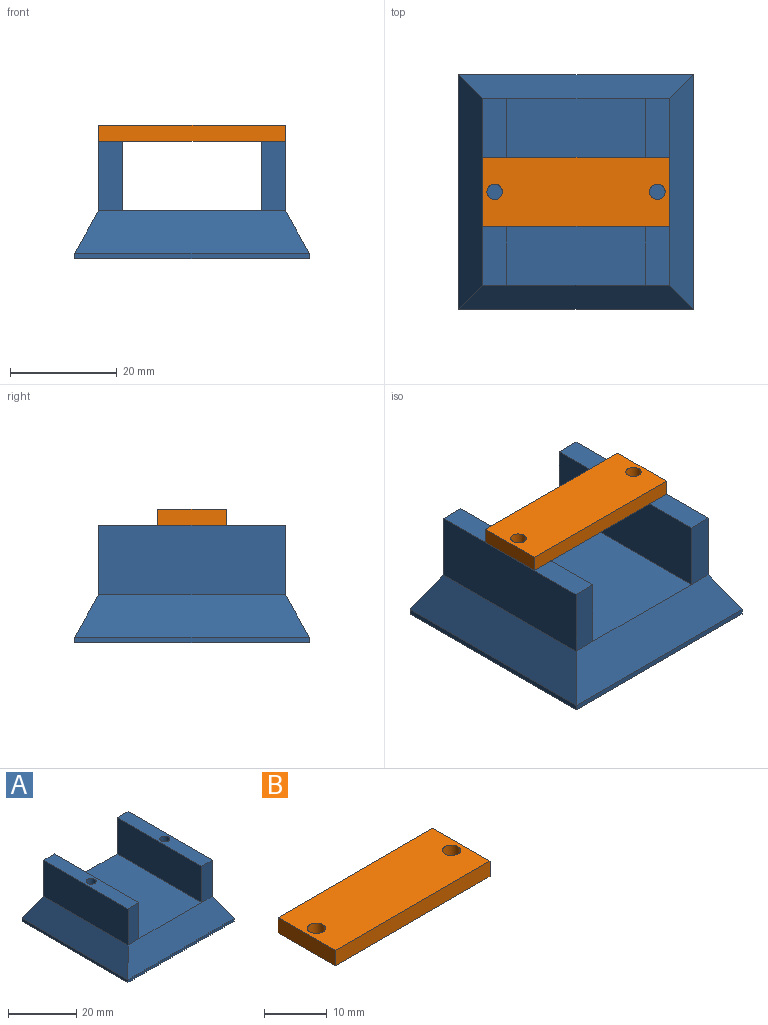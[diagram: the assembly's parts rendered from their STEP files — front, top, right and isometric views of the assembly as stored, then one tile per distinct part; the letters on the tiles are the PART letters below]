
ASSEMBLY  parts=2 mates=1
PART A: 33 faces, bbox 44x44x22 mm
  f0: plane 35x26mm, normal (0,0,1), area 910mm2, adj f7,f8,f19,f25
  f1: plane 44x1mm, normal (-1,0,0), area 44mm2, adj f2,f4,f5,f6
  f2: plane 44x1mm, normal (0,-1,0), area 44mm2, adj f1,f3,f5,f8
  f3: plane 44x1mm, normal (1,0,0), area 44mm2, adj f2,f4,f5,f9
  f4: plane 44x1mm, normal (0,1,0), area 44mm2, adj f1,f3,f5,f7
  f5: plane 44x44mm, normal (0,0,-1), area 492mm2, adj f1,f2,f3,f4,f10,f11,f12,f13
  f6: plane 44x8mm, normal (-0.87,0,0.49), area 362.6mm2, adj f1,f7,f8,f27
  f7: plane 44x8mm, normal (0,0.87,0.49), area 362.6mm2, adj f0,f4,f6,f9,f22,f26
  f8: plane 44x8mm, normal (0,-0.87,0.49), area 362.6mm2, adj f0,f2,f6,f9,f20,f24
  f9: plane 44x8mm, normal (0.87,0,0.49), area 362.6mm2, adj f3,f7,f8,f21
  f10: plane 38x0.21mm, normal (1,0,0), area 8.1mm2, adj f5,f11,f13,f15
  f11: plane 38x0.21mm, normal (0,1,0), area 8.1mm2, adj f5,f10,f12,f17
  f12: plane 38x0.21mm, normal (-1,0,0), area 8.1mm2, adj f5,f11,f13,f18
  f13: plane 38x0.21mm, normal (0,-1,0), area 8.1mm2, adj f5,f10,f12,f16
  f14: plane 31.49x31.49mm, normal (0,0,-1), area 991.7mm2, adj f15,f16,f17,f18
  f15: plane 38x5.79mm, normal (0.87,0,-0.49), area 230.7mm2, adj f10,f14,f16,f17
  f16: plane 38x5.79mm, normal (0,-0.87,-0.49), area 230.7mm2, adj f13,f14,f15,f18
  f17: plane 38x5.79mm, normal (0,0.87,-0.49), area 230.7mm2, adj f11,f14,f15,f18
  f18: plane 38x5.79mm, normal (-0.87,0,-0.49), area 230.7mm2, adj f12,f14,f16,f17
  f19: plane 35x13mm, normal (-1,0,0), area 455mm2, adj f0,f20,f22,f23
  f20: plane 13x4.5mm, normal (0,-1,0), area 58.5mm2, adj f8,f19,f21,f23
  f21: plane 35x13mm, normal (1,0,0), area 455mm2, adj f9,f20,f22,f23
  f22: plane 13x4.5mm, normal (0,1,0), area 58.5mm2, adj f7,f19,f21,f23
  f23: plane 35x4.5mm, normal (0,0,1), area 150.9mm2, adj f19,f20,f21,f22,f31
  f24: plane 13x4.5mm, normal (0,-1,0), area 58.5mm2, adj f8,f25,f27,f28
  f25: plane 35x13mm, normal (1,0,0), area 455mm2, adj f0,f24,f26,f28
  f26: plane 13x4.5mm, normal (0,1,0), area 58.5mm2, adj f7,f25,f27,f28
  f27: plane 35x13mm, normal (-1,0,0), area 455mm2, adj f6,f24,f26,f28
  f28: plane 35x4.5mm, normal (0,0,1), area 150.9mm2, adj f24,f25,f26,f27,f29
  f29: cylinder r=1.45mm len=13mm, axis (0,0,1), area 118.4mm2, adj f28,f30
  f30: plane 2.9x2.9mm, normal (0,0,1), area 6.6mm2, adj f29
  f31: cylinder r=1.45mm len=13mm, axis (0,0,1), area 118.4mm2, adj f23,f32
  f32: plane 2.9x2.9mm, normal (0,0,1), area 6.6mm2, adj f31
PART B: 8 faces, bbox 35x12.9x3 mm
  f0: plane 35x3mm, normal (0,-1,0), area 105mm2, adj f1,f5,f6,f7
  f1: plane 12.88x3mm, normal (1,0,0), area 38.6mm2, adj f0,f2,f6,f7
  f2: plane 35x3mm, normal (0,1,0), area 105mm2, adj f1,f5,f6,f7
  f3: cylinder r=1.45mm len=3mm, axis (0,0,-1), area 27.3mm2, adj f6,f7
  f4: cylinder r=1.45mm len=3mm, axis (0,0,-1), area 27.3mm2, adj f6,f7
  f5: plane 12.88x3mm, normal (-1,0,0), area 38.6mm2, adj f0,f2,f6,f7
  f6: plane 35x12.88mm, normal (0,0,1), area 437.5mm2, adj f0,f1,f2,f3,f4,f5
  f7: plane 35x12.88mm, normal (0,0,-1), area 437.5mm2, adj f0,f1,f2,f3,f4,f5
PLACE A t=(-46.6,-30.8,-26.12)mm
PLACE B t=(-4.95,3.01,-4.12)mm
MATE slider A.f29 <-> B.f3  axis (0,0,1) through (-58.7,-20.68,-4.12)mm
